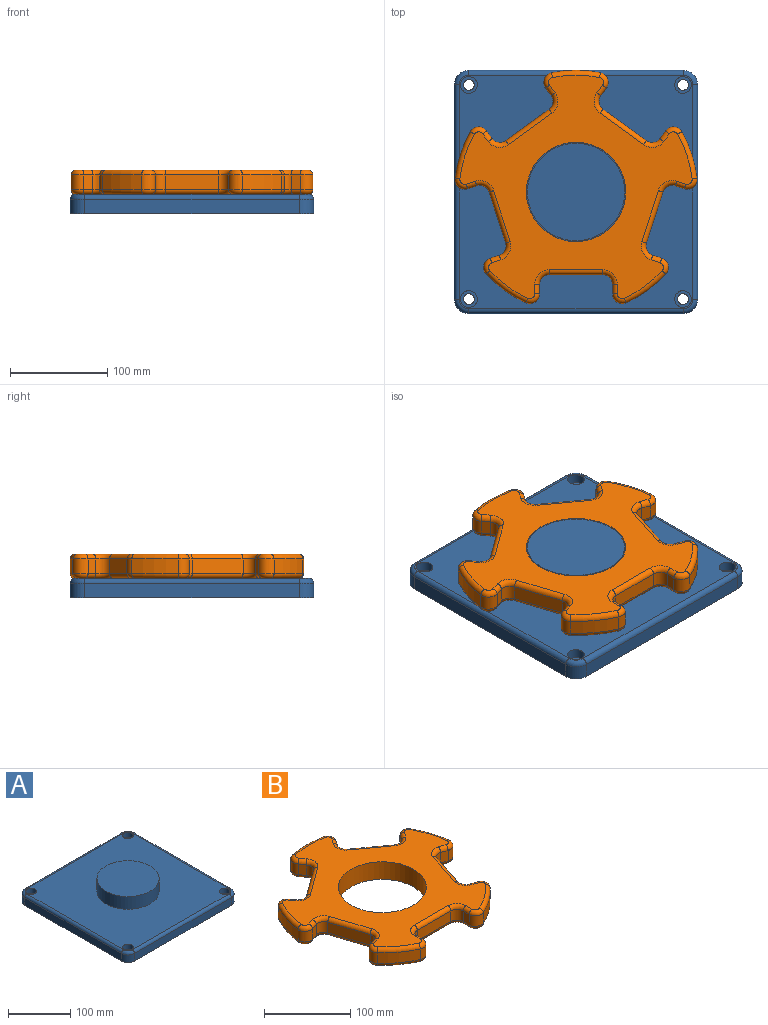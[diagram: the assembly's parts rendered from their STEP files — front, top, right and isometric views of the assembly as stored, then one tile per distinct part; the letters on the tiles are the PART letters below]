
ASSEMBLY  parts=2 mates=1
PART A: 32 faces, bbox 252.5x252.5x45 mm
  f0: plane 220x15mm, normal (1,0,0), area 3300mm2, adj f5,f8,f11,f27
  f1: plane 220x15mm, normal (0,1,0), area 3300mm2, adj f5,f8,f9,f31
  f2: plane 220x15mm, normal (-1,0,0), area 3300mm2, adj f5,f9,f10,f28
  f3: plane 220x15mm, normal (0,-1,0), area 3300mm2, adj f5,f10,f11,f24
  f4: plane 240x240mm, normal (0,0,1), area 48725.4mm2, adj f6,f14,f17,f20,f23,f24,f25,f26
  f5: plane 250x250mm, normal (0,0,-1), area 61926.7mm2, adj f0,f1,f2,f3,f8,f9,f10,f11
  f6: cylinder r=50mm len=100mm, axis (0,0,-1), area 7854mm2, adj f4,f7
  f7: plane 100x100mm, normal (0,0,1), area 7854mm2, adj f6
  f8: cylinder r=15mm len=15mm, axis (0,0,-1), area 353.4mm2, adj f0,f1,f5,f29
  f9: cylinder r=15mm len=15mm, axis (0,0,1), area 353.4mm2, adj f1,f2,f5,f30
  f10: cylinder r=15mm len=15mm, axis (0,0,-1), area 353.4mm2, adj f2,f3,f5,f26
  f11: cylinder r=15mm len=15mm, axis (0,0,1), area 353.4mm2, adj f0,f3,f5,f25
  f12: cylinder r=5.5mm len=11mm, axis (0,0,1), area 345.6mm2, adj f5,f13
  f13: plane 17.25x17.25mm, normal (0,0,1), area 138.7mm2, adj f12,f14
  f14: cylinder r=8.62mm len=17.25mm, axis (0,0,1), area 541.9mm2, adj f4,f13
  f15: cylinder r=5.5mm len=11mm, axis (0,0,1), area 345.6mm2, adj f5,f16
  f16: plane 17.25x17.25mm, normal (0,0,1), area 138.7mm2, adj f15,f17
  f17: cylinder r=8.62mm len=17.25mm, axis (0,0,1), area 541.9mm2, adj f4,f16
  f18: cylinder r=5.5mm len=11mm, axis (0,0,1), area 345.6mm2, adj f5,f19
  f19: plane 17.25x17.25mm, normal (0,0,1), area 138.7mm2, adj f18,f20
  f20: cylinder r=8.62mm len=17.25mm, axis (0,0,1), area 541.9mm2, adj f4,f19
  f21: cylinder r=5.5mm len=11mm, axis (0,0,1), area 345.6mm2, adj f5,f22
  f22: plane 17.25x17.25mm, normal (0,0,1), area 138.7mm2, adj f21,f23
  f23: cylinder r=8.62mm len=17.25mm, axis (0,0,1), area 541.9mm2, adj f4,f22
  f24: cylinder r=5mm len=220mm, axis (-1,0,0), area 1727.9mm2, adj f3,f4,f25,f26
  f25: torus R=10mm, axis (0,0,1), area 162.6mm2, adj f4,f11,f24,f27
  f26: torus R=10mm, axis (0,0,1), area 162.6mm2, adj f4,f10,f24,f28
  f27: cylinder r=5mm len=220mm, axis (0,-1,0), area 1727.9mm2, adj f0,f4,f25,f29
  f28: cylinder r=5mm len=220mm, axis (0,1,0), area 1727.9mm2, adj f2,f4,f26,f30
  f29: torus R=10mm, axis (0,0,1), area 162.6mm2, adj f4,f8,f27,f31
  f30: torus R=10mm, axis (0,0,1), area 162.6mm2, adj f4,f9,f28,f31
  f31: cylinder r=5mm len=220mm, axis (1,0,0), area 1727.9mm2, adj f1,f4,f29,f30
PART B: 123 faces, bbox 268.9x258.5x25 mm
  f0: plane 238.57x229.73mm, normal (0,0,1), area 21505.7mm2, adj f6,f43,f44,f45,f46,f47,f48,f49
  f1: plane 238.57x229.73mm, normal (0,0,-1), area 21505.7mm2, adj f6,f83,f84,f85,f86,f87,f88,f89
  f2: cylinder r=125mm len=40.68mm, axis (0,0,-1), area 759.5mm2, adj f13,f42,f51,f91
  f3: cylinder r=125mm len=47.82mm, axis (0,0,-1), area 759.5mm2, adj f35,f41,f67,f107
  f4: cylinder r=125mm len=50.29mm, axis (0,0,-1), area 759.5mm2, adj f28,f34,f82,f122
  f5: cylinder r=125mm len=47.82mm, axis (0,0,-1), area 759.5mm2, adj f21,f27,f66,f106
  f6: cylinder r=51mm len=102mm, axis (0,0,-1), area 8011.1mm2, adj f0,f1
  f7: cylinder r=125mm len=40.68mm, axis (0,0,-1), area 759.5mm2, adj f14,f20,f50,f90
  f8: plane 15x9.73mm, normal (-1,0,0), area 146mm2, adj f11,f14,f46,f86
  f9: plane 55x15mm, normal (0,-1,0), area 825mm2, adj f11,f12,f43,f83
  f10: plane 15x9.73mm, normal (1,0,0), area 146mm2, adj f12,f13,f47,f87
  f11: cylinder r=10mm len=15mm, axis (0,0,-1), area 235.6mm2, adj f8,f9,f44,f84
  f12: cylinder r=10mm len=15mm, axis (0,0,-1), area 235.6mm2, adj f9,f10,f45,f85
  f13: cylinder r=10mm len=15mm, axis (0,0,-1), area 299.5mm2, adj f2,f10,f49,f89
  f14: cylinder r=10mm len=15mm, axis (0,0,-1), area 299.5mm2, adj f7,f8,f48,f88
  f15: plane 15x9.26mm, normal (-0.31,-0.95,0), area 146mm2, adj f18,f21,f62,f102
  f16: plane 52.31x17mm, normal (0.95,-0.31,0), area 825mm2, adj f18,f19,f58,f98
  f17: plane 15x9.26mm, normal (0.31,0.95,0), area 146mm2, adj f19,f20,f54,f94
  f18: cylinder r=10mm len=15mm, axis (0,0,-1), area 235.6mm2, adj f15,f16,f60,f100
  f19: cylinder r=10mm len=15mm, axis (0,0,-1), area 235.6mm2, adj f16,f17,f56,f96
  f20: cylinder r=10mm len=16.25mm, axis (0,0,-1), area 299.5mm2, adj f7,f17,f52,f92
  f21: cylinder r=10mm len=15mm, axis (0,0,-1), area 299.5mm2, adj f5,f15,f64,f104
  f22: plane 15x7.87mm, normal (0.81,-0.59,0), area 146mm2, adj f25,f28,f78,f118
  f23: plane 44.5x32.33mm, normal (0.59,0.81,0), area 825mm2, adj f25,f26,f74,f114
  f24: plane 15x7.87mm, normal (-0.81,0.59,0), area 146mm2, adj f26,f27,f70,f110
  f25: cylinder r=10mm len=15mm, axis (0,0,-1), area 235.6mm2, adj f22,f23,f76,f116
  f26: cylinder r=10mm len=15mm, axis (0,0,-1), area 235.6mm2, adj f23,f24,f72,f112
  f27: cylinder r=10mm len=16.78mm, axis (0,0,-1), area 299.5mm2, adj f5,f24,f68,f108
  f28: cylinder r=10mm len=15.67mm, axis (0,0,-1), area 299.5mm2, adj f4,f22,f80,f120
  f29: plane 15x7.87mm, normal (0.81,0.59,0), area 146mm2, adj f32,f35,f71,f111
  f30: plane 44.5x32.33mm, normal (-0.59,0.81,0), area 825mm2, adj f32,f33,f75,f115
  f31: plane 15x7.87mm, normal (-0.81,-0.59,0), area 146mm2, adj f33,f34,f79,f119
  f32: cylinder r=10mm len=15mm, axis (0,0,-1), area 235.6mm2, adj f29,f30,f73,f113
  f33: cylinder r=10mm len=15mm, axis (0,0,-1), area 235.6mm2, adj f30,f31,f77,f117
  f34: cylinder r=10mm len=15.67mm, axis (0,0,-1), area 299.5mm2, adj f4,f31,f81,f121
  f35: cylinder r=10mm len=16.78mm, axis (0,0,-1), area 299.5mm2, adj f3,f29,f69,f109
  f36: plane 15x9.26mm, normal (-0.31,0.95,0), area 146mm2, adj f39,f42,f55,f95
  f37: plane 52.31x17mm, normal (-0.95,-0.31,0), area 825mm2, adj f39,f40,f59,f99
  f38: plane 15x9.26mm, normal (0.31,-0.95,0), area 146mm2, adj f40,f41,f63,f103
  f39: cylinder r=10mm len=15mm, axis (0,0,-1), area 235.6mm2, adj f36,f37,f57,f97
  f40: cylinder r=10mm len=15mm, axis (0,0,-1), area 235.6mm2, adj f37,f38,f61,f101
  f41: cylinder r=10mm len=15mm, axis (0,0,-1), area 299.5mm2, adj f3,f38,f65,f105
  f42: cylinder r=10mm len=16.25mm, axis (0,0,-1), area 299.5mm2, adj f2,f36,f53,f93
  f43: cylinder r=5mm len=55mm, axis (1,0,0), area 432mm2, adj f0,f9,f44,f45
  f44: torus R=15mm, axis (0,0,1), area 145.8mm2, adj f0,f11,f43,f46
  f45: torus R=15mm, axis (0,0,1), area 145.8mm2, adj f0,f12,f43,f47
  f46: cylinder r=5mm len=9.73mm, axis (0,-1,0), area 76.4mm2, adj f0,f8,f44,f48
  f47: cylinder r=5mm len=9.73mm, axis (0,1,0), area 76.4mm2, adj f0,f10,f45,f49
  f48: torus R=5mm, axis (0,0,1), area 128.3mm2, adj f0,f14,f46,f50
  f49: torus R=5mm, axis (0,0,1), area 128.3mm2, adj f0,f13,f47,f51
  f50: torus R=120mm, axis (0,0,1), area 391.9mm2, adj f0,f7,f48,f52
  f51: torus R=120mm, axis (0,0,1), area 391.9mm2, adj f0,f2,f49,f53
  f52: torus R=5mm, axis (0,0,1), area 128.3mm2, adj f0,f20,f50,f54
  f53: torus R=5mm, axis (0,0,1), area 128.3mm2, adj f0,f42,f51,f55
  f54: cylinder r=5mm len=10.8mm, axis (-0.95,0.31,0), area 76.4mm2, adj f0,f17,f52,f56
  f55: cylinder r=5mm len=10.8mm, axis (-0.95,-0.31,0), area 76.4mm2, adj f0,f36,f53,f57
  f56: torus R=15mm, axis (0,0,1), area 145.8mm2, adj f0,f19,f54,f58
  f57: torus R=15mm, axis (0,0,1), area 145.8mm2, adj f0,f39,f55,f59
  f58: cylinder r=5mm len=53.85mm, axis (0.31,0.95,0), area 432mm2, adj f0,f16,f56,f60
  f59: cylinder r=5mm len=53.85mm, axis (0.31,-0.95,0), area 432mm2, adj f0,f37,f57,f61
  f60: torus R=15mm, axis (0,0,1), area 145.8mm2, adj f0,f18,f58,f62
  f61: torus R=15mm, axis (0,0,1), area 145.8mm2, adj f0,f40,f59,f63
  f62: cylinder r=5mm len=10.8mm, axis (0.95,-0.31,0), area 76.4mm2, adj f0,f15,f60,f64
  f63: cylinder r=5mm len=10.8mm, axis (0.95,0.31,0), area 76.4mm2, adj f0,f38,f61,f65
  f64: torus R=5mm, axis (0,0,1), area 128.3mm2, adj f0,f21,f62,f66
  f65: torus R=5mm, axis (0,0,1), area 128.3mm2, adj f0,f41,f63,f67
  f66: torus R=120mm, axis (0,0,1), area 391.9mm2, adj f0,f5,f64,f68
  f67: torus R=120mm, axis (0,0,1), area 391.9mm2, adj f0,f3,f65,f69
  f68: torus R=5mm, axis (0,0,1), area 128.3mm2, adj f0,f27,f66,f70
  f69: torus R=5mm, axis (0,0,1), area 128.3mm2, adj f0,f35,f67,f71
  f70: cylinder r=5mm len=10.81mm, axis (-0.59,-0.81,0), area 76.4mm2, adj f0,f24,f68,f72
  f71: cylinder r=5mm len=10.81mm, axis (-0.59,0.81,0), area 76.4mm2, adj f0,f29,f69,f73
  f72: torus R=15mm, axis (0,0,1), area 145.8mm2, adj f0,f26,f70,f74
  f73: torus R=15mm, axis (0,0,1), area 145.8mm2, adj f0,f32,f71,f75
  f74: cylinder r=5mm len=47.44mm, axis (-0.81,0.59,0), area 432mm2, adj f0,f23,f72,f76
  f75: cylinder r=5mm len=47.44mm, axis (-0.81,-0.59,0), area 432mm2, adj f0,f30,f73,f77
  f76: torus R=15mm, axis (0,0,1), area 145.8mm2, adj f0,f25,f74,f78
  f77: torus R=15mm, axis (0,0,1), area 145.8mm2, adj f0,f33,f75,f79
  f78: cylinder r=5mm len=10.81mm, axis (0.59,0.81,0), area 76.4mm2, adj f0,f22,f76,f80
  f79: cylinder r=5mm len=10.81mm, axis (0.59,-0.81,0), area 76.4mm2, adj f0,f31,f77,f81
  f80: torus R=5mm, axis (0,0,1), area 128.3mm2, adj f0,f28,f78,f82
  f81: torus R=5mm, axis (0,0,1), area 128.3mm2, adj f0,f34,f79,f82
  f82: torus R=120mm, axis (0,0,1), area 391.9mm2, adj f0,f4,f80,f81
  f83: cylinder r=5mm len=55mm, axis (-1,0,0), area 432mm2, adj f1,f9,f84,f85
  f84: torus R=15mm, axis (0,0,1), area 145.8mm2, adj f1,f11,f83,f86
  f85: torus R=15mm, axis (0,0,1), area 145.8mm2, adj f1,f12,f83,f87
  f86: cylinder r=5mm len=9.73mm, axis (0,1,0), area 76.4mm2, adj f1,f8,f84,f88
  f87: cylinder r=5mm len=9.73mm, axis (0,-1,0), area 76.4mm2, adj f1,f10,f85,f89
  f88: torus R=5mm, axis (0,0,1), area 128.3mm2, adj f1,f14,f86,f90
  f89: torus R=5mm, axis (0,0,1), area 128.3mm2, adj f1,f13,f87,f91
  f90: torus R=120mm, axis (0,0,1), area 391.9mm2, adj f1,f7,f88,f92
  f91: torus R=120mm, axis (0,0,1), area 391.9mm2, adj f1,f2,f89,f93
  f92: torus R=5mm, axis (0,0,1), area 128.3mm2, adj f1,f20,f90,f94
  f93: torus R=5mm, axis (0,0,1), area 128.3mm2, adj f1,f42,f91,f95
  f94: cylinder r=5mm len=10.8mm, axis (0.95,-0.31,0), area 76.4mm2, adj f1,f17,f92,f96
  f95: cylinder r=5mm len=10.8mm, axis (0.95,0.31,0), area 76.4mm2, adj f1,f36,f93,f97
  f96: torus R=15mm, axis (0,0,1), area 145.8mm2, adj f1,f19,f94,f98
  f97: torus R=15mm, axis (0,0,1), area 145.8mm2, adj f1,f39,f95,f99
  f98: cylinder r=5mm len=53.85mm, axis (-0.31,-0.95,0), area 432mm2, adj f1,f16,f96,f100
  f99: cylinder r=5mm len=53.85mm, axis (-0.31,0.95,0), area 432mm2, adj f1,f37,f97,f101
  f100: torus R=15mm, axis (0,0,1), area 145.8mm2, adj f1,f18,f98,f102
  f101: torus R=15mm, axis (0,0,1), area 145.8mm2, adj f1,f40,f99,f103
  f102: cylinder r=5mm len=10.8mm, axis (-0.95,0.31,0), area 76.4mm2, adj f1,f15,f100,f104
  f103: cylinder r=5mm len=10.8mm, axis (-0.95,-0.31,0), area 76.4mm2, adj f1,f38,f101,f105
  f104: torus R=5mm, axis (0,0,1), area 128.3mm2, adj f1,f21,f102,f106
  f105: torus R=5mm, axis (0,0,1), area 128.3mm2, adj f1,f41,f103,f107
  f106: torus R=120mm, axis (0,0,1), area 391.9mm2, adj f1,f5,f104,f108
  f107: torus R=120mm, axis (0,0,1), area 391.9mm2, adj f1,f3,f105,f109
  f108: torus R=5mm, axis (0,0,1), area 128.3mm2, adj f1,f27,f106,f110
  f109: torus R=5mm, axis (0,0,1), area 128.3mm2, adj f1,f35,f107,f111
  f110: cylinder r=5mm len=10.81mm, axis (0.59,0.81,0), area 76.4mm2, adj f1,f24,f108,f112
  f111: cylinder r=5mm len=10.81mm, axis (0.59,-0.81,0), area 76.4mm2, adj f1,f29,f109,f113
  f112: torus R=15mm, axis (0,0,1), area 145.8mm2, adj f1,f26,f110,f114
  f113: torus R=15mm, axis (0,0,1), area 145.8mm2, adj f1,f32,f111,f115
  f114: cylinder r=5mm len=47.44mm, axis (0.81,-0.59,0), area 432mm2, adj f1,f23,f112,f116
  f115: cylinder r=5mm len=47.44mm, axis (0.81,0.59,0), area 432mm2, adj f1,f30,f113,f117
  f116: torus R=15mm, axis (0,0,1), area 145.8mm2, adj f1,f25,f114,f118
  f117: torus R=15mm, axis (0,0,1), area 145.8mm2, adj f1,f33,f115,f119
  f118: cylinder r=5mm len=10.81mm, axis (-0.59,-0.81,0), area 76.4mm2, adj f1,f22,f116,f120
  f119: cylinder r=5mm len=10.81mm, axis (-0.59,0.81,0), area 76.4mm2, adj f1,f31,f117,f121
  f120: torus R=5mm, axis (0,0,1), area 128.3mm2, adj f1,f28,f118,f122
  f121: torus R=5mm, axis (0,0,1), area 128.3mm2, adj f1,f34,f119,f122
  f122: torus R=120mm, axis (0,0,1), area 391.9mm2, adj f1,f4,f120,f121
PLACE A at identity fixed
PLACE B at identity
MATE revolute B.f2 <-> A.f6  axis (0,0,1) through (0,0,45)mm
